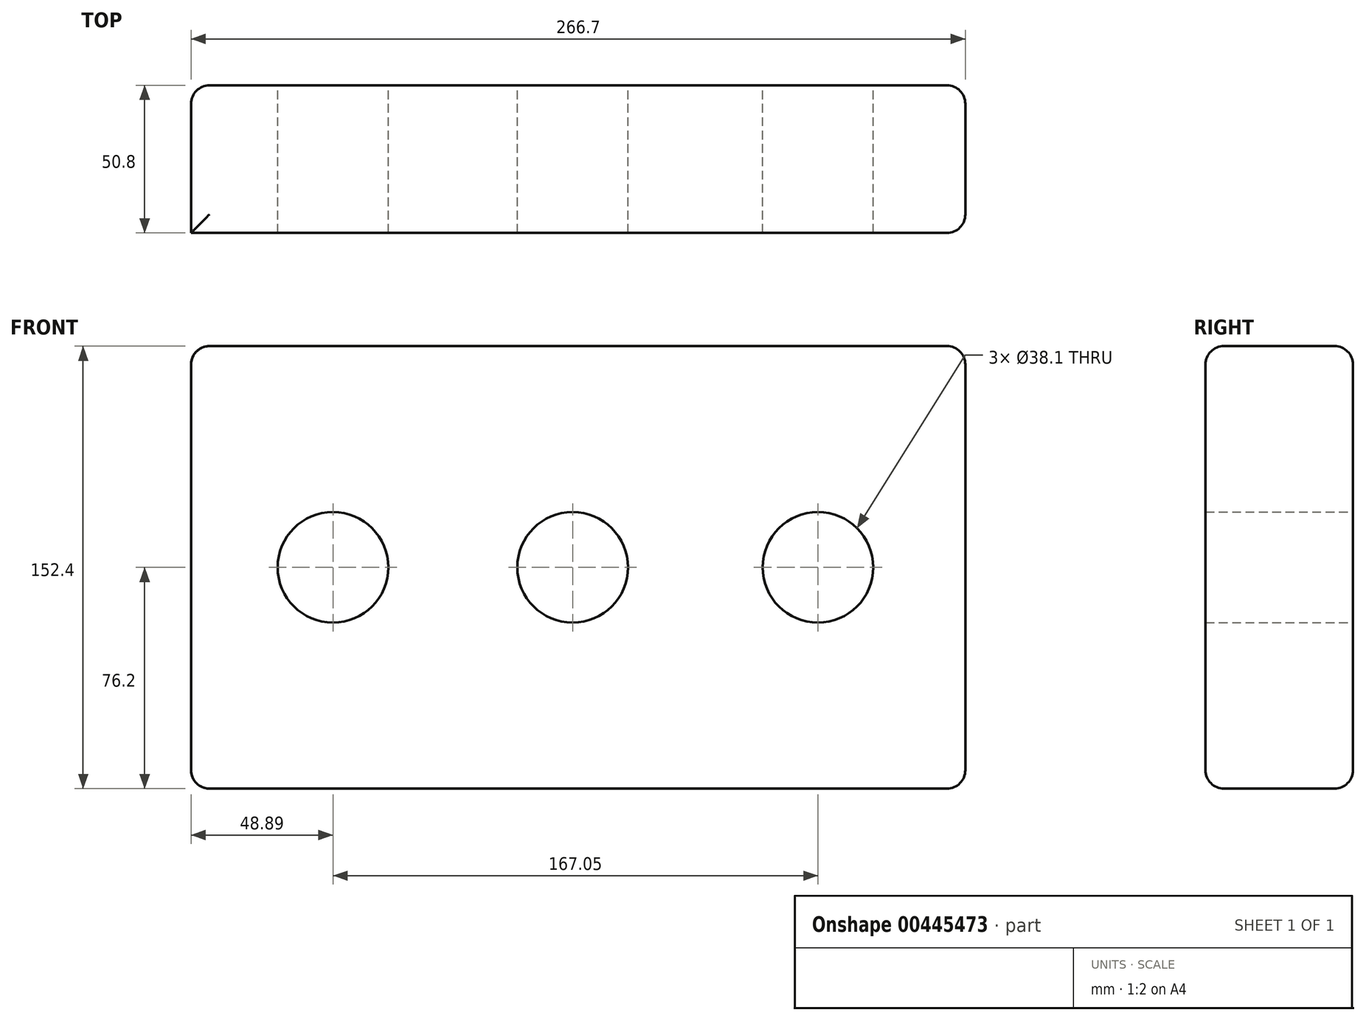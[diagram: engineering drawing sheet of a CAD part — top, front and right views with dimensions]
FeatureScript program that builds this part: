
annotation { "Feature Type Name" : "Feature", "Feature Type Description" : "" }
export const myFeature = defineFeature(function(context is Context, id is Id, definition is map)
    precondition{}
    {
        {
            var Q0;
            Q0=qCreatedBy(makeId("Front.planeOp"),FACE);
            var sketch = newSketch(context, id + "F0", { "sketchPlane" : qUnion([Q0])});
            skLineSegment(sketch, "E0.bottom", {"start": v(-131.44, 76.2) * mm, "end": v(135.26, 76.2) * mm});
            skLineSegment(sketch, "E0.top", {"start": v(-131.44, -76.2) * mm, "end": v(135.26, -76.2) * mm});
            skLineSegment(sketch, "E0.left", {"start": v(-131.44, 76.2) * mm, "end": v(-131.44, -76.2) * mm});
            skLineSegment(sketch, "E0.right", {"start": v(135.26, 76.2) * mm, "end": v(135.26, -76.2) * mm});
            skPoint(sketch, "E0.middle", {"position": v(1.9, 0) * mm});
            skCircle(sketch, "E1", {"center": v(0, 0) * mm, "radius": 19.05 * mm});
            skLineSegment(sketch, "E2", {"start": v(-19.05, 0) * mm, "end": v(-82.55, 0) * mm});
            skLineSegment(sketch, "E3", {"start": v(19.05, 0) * mm, "end": v(82.55, 0) * mm});
            skCircle(sketch, "E4", {"center": v(-82.55, 0) * mm, "radius": 19.05 * mm});
            skCircle(sketch, "E5", {"center": v(84.5, 0) * mm, "radius": 19.05 * mm});
            skSolve(sketch);
        }
        {
            var Q0;
            Q0=makeQuery(id+"F0.imprint","IMPRINT",FACE,{"disambiguationData":[TD([[makeQuery(id+"F0.imprint","IMPRINT",EDGE,{"derivedFrom":sQuery(id+"F0.wireOp",EDGE,"E0.bottom")}),-1.0]])]});
            extrude(context, id + "F1", {"entities" : qUnion([Q0]), "depth" : 50.8 * mm});
        }
        {
            var Q0;
            Q0=makeQuery(id+"F1.opExtrude","CAP_EDGE",EDGE,{"disambiguationData":[OSD([sQuery(id+"F0.wireOp",EDGE,"E0.top")])],"isStart":false});
            var Q1;
            Q1=makeQuery(id+"F1.opExtrude","SWEPT_FACE",FACE,{"disambiguationData":[OSD([sQuery(id+"F0.wireOp",EDGE,"E0.top")])]});
            var Q2;
            Q2=makeQuery(id+"F1.opExtrude","CAP_EDGE",EDGE,{"disambiguationData":[OSD([sQuery(id+"F0.wireOp",EDGE,"E0.left")])],"isStart":true});
            var Q3;
            Q3=makeQuery(id+"F1.opExtrude","SWEPT_FACE",FACE,{"disambiguationData":[OSD([sQuery(id+"F0.wireOp",EDGE,"E0.bottom")])]});
            var Q4;
            Q4=makeQuery(id+"F1.opExtrude","SWEPT_FACE",FACE,{"disambiguationData":[OSD([sQuery(id+"F0.wireOp",EDGE,"E0.right")])]});
            fillet(context, id + "F2", {"entities" : qUnion([Q0, Q1, Q2, Q3, Q4]), "radius" : 6.35 * mm, "tangentPropagation" : true, "allowEdgeOverflow" : false});
        }
    });
